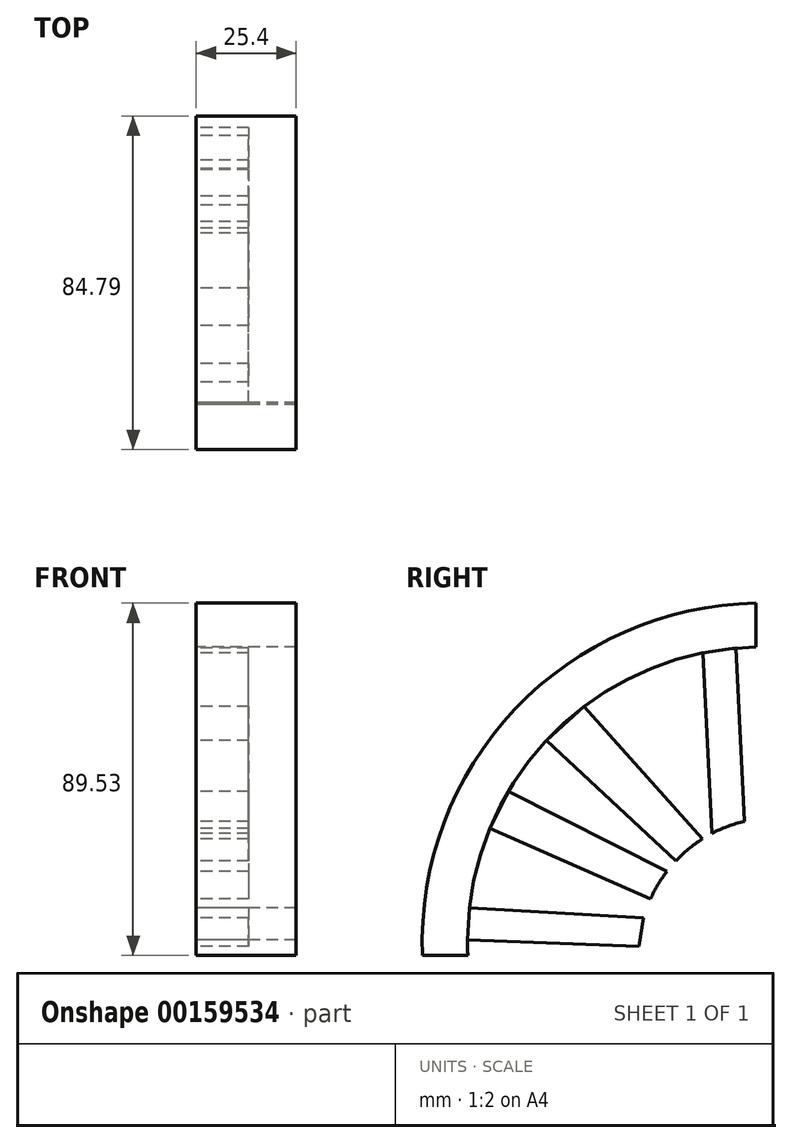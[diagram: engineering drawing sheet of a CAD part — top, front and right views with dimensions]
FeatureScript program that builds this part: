
annotation { "Feature Type Name" : "Feature", "Feature Type Description" : "" }
export const myFeature = defineFeature(function(context is Context, id is Id, definition is map)
    precondition{}
    {
        {
            var Q0;
            Q0=qCreatedBy(makeId("Right.planeOp"),FACE);
            var sketch = newSketch(context, id + "F0", { "sketchPlane" : qUnion([Q0])});
            skLineSegment(sketch, "E0", {"start": v(30.13, -13.76) * mm, "end": v(30.13, 52.28) * mm});
            skArc(sketch, "E1", {"start": v(30.13, 52.28) * mm, "mid": v(-31.07, 25.35) * mm, "end": v(-54.6, -37.25) * mm});
            skLineSegment(sketch, "E2", {"start": v(30.13, 52.28) * mm, "end": v(30.13, 41.1) * mm});
            skLineSegment(sketch, "E3", {"start": v(30.13, -13.76) * mm, "end": v(30.13, -2.58) * mm});
            skArc(sketch, "E4", {"start": v(30.13, 41.1) * mm, "mid": v(-23.07, 17.44) * mm, "end": v(-43.06, -37.25) * mm});
            skArc(sketch, "E5", {"start": v(30.13, -13.76) * mm, "mid": v(15.63, -21.41) * mm, "end": v(11.38, -37.25) * mm});
            skLineSegment(sketch, "E6", {"start": v(-43.16, -33.27) * mm, "end": v(0.35, -34.94) * mm});
            skLineSegment(sketch, "E7", {"start": v(-42.69, -25.13) * mm, "end": v(1.6, -27.62) * mm});
            skLineSegment(sketch, "E8", {"start": v(-37.5, -4.96) * mm, "end": v(3.36, -22.82) * mm});
            skLineSegment(sketch, "E9", {"start": v(-32.76, 4.5) * mm, "end": v(7.51, -15.88) * mm});
            skLineSegment(sketch, "E10", {"start": v(27.2, -3.14) * mm, "end": v(25.09, 40.85) * mm});
            skLineSegment(sketch, "E11", {"start": v(9.77, -13.22) * mm, "end": v(-23.07, 17.44) * mm});
            skLineSegment(sketch, "E12", {"start": v(-13.57, 26.01) * mm, "end": v(16.56, -7.62) * mm});
            skLineSegment(sketch, "E13", {"start": v(18.9, -6.26) * mm, "end": v(16.7, 39.65) * mm});
            skLineSegment(sketch, "E14", {"start": v(0.35, -34.94) * mm, "end": v(1.6, -27.62) * mm});
            skLineSegment(sketch, "E15", {"start": v(-42.69, -25.13) * mm, "end": v(-43.16, -33.27) * mm});
            skLineSegment(sketch, "E16", {"start": v(-32.76, 4.5) * mm, "end": v(-37.5, -4.96) * mm});
            skLineSegment(sketch, "E17", {"start": v(7.51, -15.88) * mm, "end": v(3.36, -22.82) * mm});
            skLineSegment(sketch, "E18", {"start": v(9.77, -13.22) * mm, "end": v(16.56, -7.62) * mm});
            skLineSegment(sketch, "E19", {"start": v(-13.57, 26.01) * mm, "end": v(-23.07, 17.44) * mm});
            skLineSegment(sketch, "E20", {"start": v(16.7, 39.65) * mm, "end": v(25.09, 40.85) * mm});
            skLineSegment(sketch, "E21", {"start": v(18.9, -6.26) * mm, "end": v(27.2, -3.14) * mm});
            skLineSegment(sketch, "E22", {"start": v(-54.6, -37.25) * mm, "end": v(-43.06, -37.25) * mm});
            skLineSegment(sketch, "E23", {"start": v(0.35, -34.94) * mm, "end": v(11.38, -37.25) * mm});
            skArc(sketch, "E24", {"start": v(30.13, -2.58) * mm, "mid": v(12.18, -10.9) * mm, "end": v(1.6, -27.62) * mm});
            skSolve(sketch);
        }
        {
            var Q0;
            {var subQ0=sQuery(id+"F0.wireOp",EDGE,"E15");Q0=makeQuery(id+"F0.imprint","IMPRINT",FACE,{"disambiguationData":[TD([[makeQuery(id+"F0.imprint","IMPRINT",EDGE,{"derivedFrom":subQ0}),-1.0]])]});}
            var Q1;
            Q1=makeQuery(id+"F0.imprint","IMPRINT",FACE,{"disambiguationData":[TD([[makeQuery(id+"F0.imprint","IMPRINT",EDGE,{"derivedFrom":sQuery(id+"F0.wireOp",EDGE,"E1")}),1.0]])]});
            var Q2;
            {var subQ4=sQuery(id+"F0.wireOp",EDGE,"E3");Q2=makeQuery(id+"F0.imprint","IMPRINT",FACE,{"disambiguationData":[TD([[makeQuery(id+"F0.imprint","IMPRINT",EDGE,{"derivedFrom":subQ4}),1.0]])]});}
            extrude(context, id + "F1", {"entities" : qUnion([Q0, Q1, Q2]), "depth" : 25.4 * mm});
        }
        {
            var Q0;
            {var subQ0=sQuery(id+"F0.wireOp",EDGE,"E11");Q0=makeQuery(id+"F0.imprint","IMPRINT",FACE,{"disambiguationData":[TD([[makeQuery(id+"F0.imprint","IMPRINT",EDGE,{"derivedFrom":subQ0}),-1.0]])]});}
            var Q1;
            {var subQ0=sQuery(id+"F0.wireOp",EDGE,"E10");Q1=makeQuery(id+"F0.imprint","IMPRINT",FACE,{"disambiguationData":[TD([[makeQuery(id+"F0.imprint","IMPRINT",EDGE,{"derivedFrom":subQ0}),1.0]])]});}
            var Q2;
            {var subQ0=sQuery(id+"F0.wireOp",EDGE,"E8");Q2=makeQuery(id+"F0.imprint","IMPRINT",FACE,{"disambiguationData":[TD([[makeQuery(id+"F0.imprint","IMPRINT",EDGE,{"derivedFrom":subQ0}),1.0]])]});}
            var Q3;
            Q3=makeQuery(id+"F0.imprint","IMPRINT",FACE,{"disambiguationData":[TD([[makeQuery(id+"F0.imprint","IMPRINT",EDGE,{"derivedFrom":sQuery(id+"F0.wireOp",EDGE,"E6")}),1.0]])]});
            extrude(context, id + "F2", {"entities" : qUnion([Q0, Q1, Q2, Q3]), "depth" : 13.33 * mm});
        }
    });
